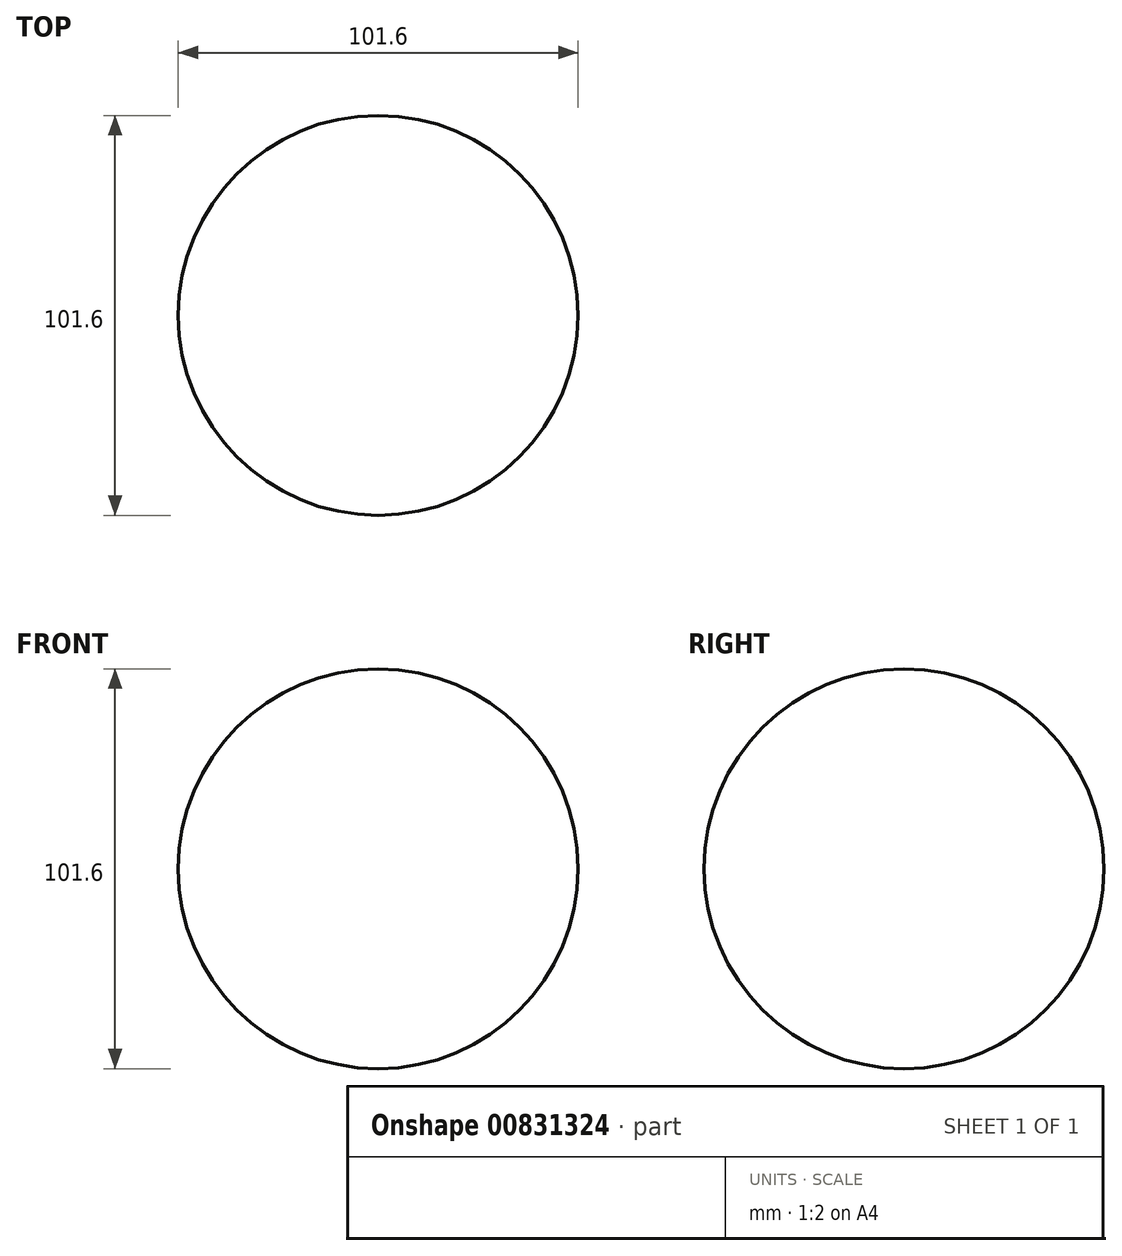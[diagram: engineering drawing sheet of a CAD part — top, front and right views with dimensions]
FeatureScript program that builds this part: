
annotation { "Feature Type Name" : "Feature", "Feature Type Description" : "" }
export const myFeature = defineFeature(function(context is Context, id is Id, definition is map)
    precondition{}
    {
        {
            var Q0;
            Q0=qCreatedBy(makeId("Top.planeOp"),FACE);
            var sketch = newSketch(context, id + "F0", { "sketchPlane" : qUnion([Q0])});
            skCircle(sketch, "E0", {"center": v(0, 0) * mm, "radius": 50.8 * mm});
            skLineSegment(sketch, "E1", {"start": v(0, -50.8) * mm, "end": v(0, 83.36) * mm});
            skSolve(sketch);
        }
        {
            var Q0;
            {var subQ0=sQuery(id+"F0.wireOp",EDGE,"E1");var subQ1=sQuery(id+"F0.wireOp",EDGE,"E0");var subQ2=makeQuery(id+"F0.imprint","INTERSECT",VERTEX,{"disambiguationData":[OD(0.0)],"derivedFrom":[subQ1,subQ0]});Q0=makeQuery(id+"F0.imprint","IMPRINT",FACE,{"disambiguationData":[TD([[makeQuery(id+"F0.imprint","IMPRINT",EDGE,{"disambiguationData":[TD([[subQ2,1.0]])],"derivedFrom":subQ1}),1.0]])]});}
            var Q1;
            Q1=sQuery(id+"F0.wireOp",EDGE,"E0");
            var Q2;
            Q2=sQuery(id+"F0.wireOp",EDGE,"E1");
            revolve(context, id + "F1", {"surfaceOperationType" : NewSurfaceOperationType.NEW, "entities" : qUnion([Q0]), "surfaceEntities" : qUnion([Q1]), "axis" : qUnion([Q2]), "revolveType" : RevolveType.FULL});
        }
    });
